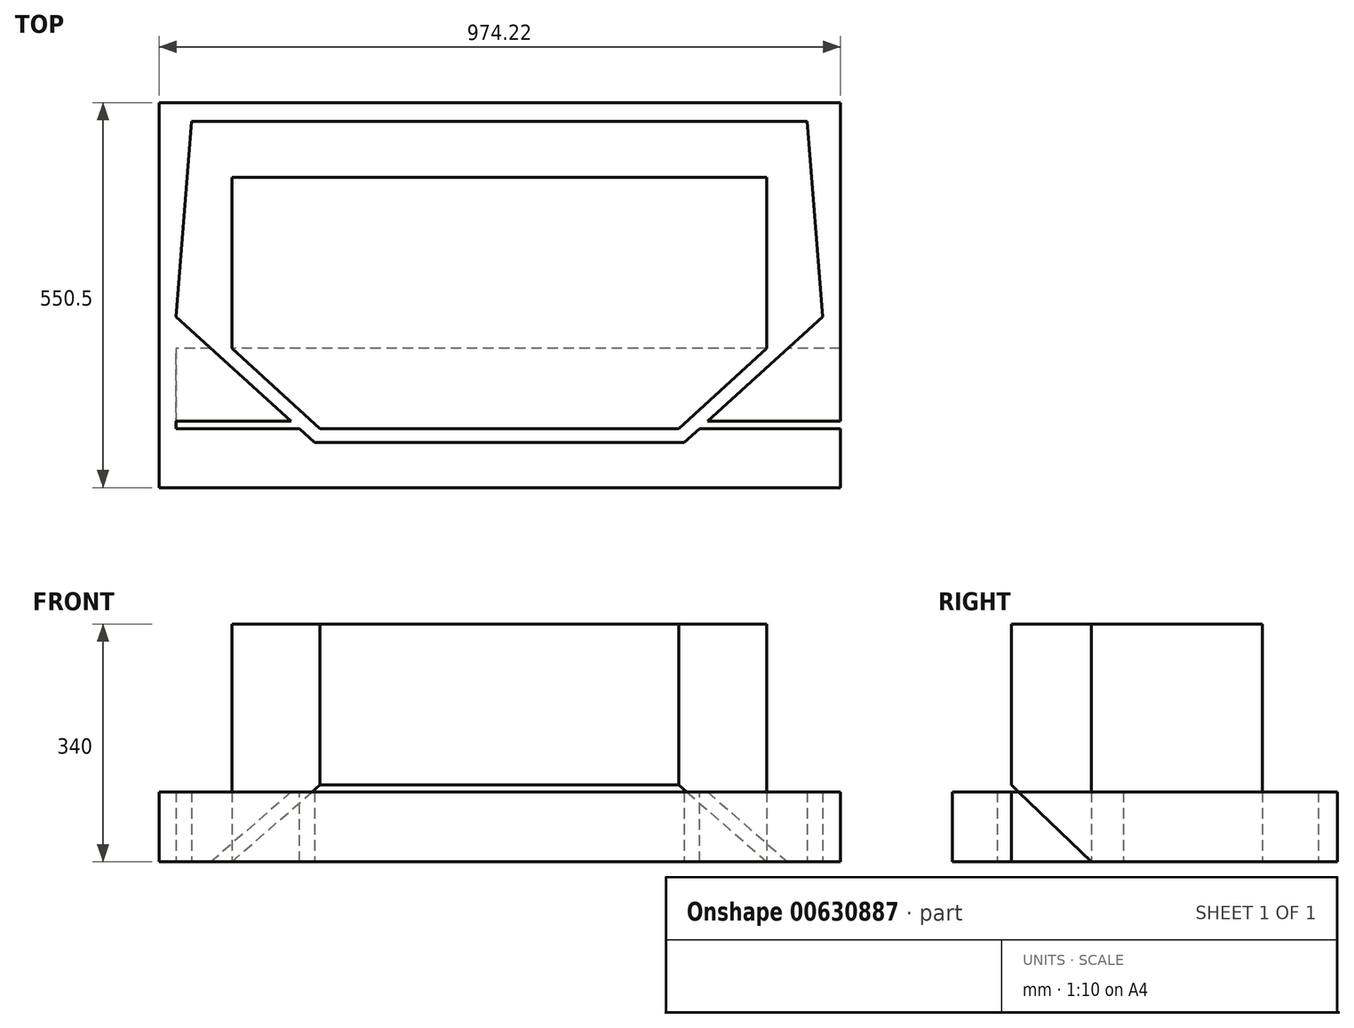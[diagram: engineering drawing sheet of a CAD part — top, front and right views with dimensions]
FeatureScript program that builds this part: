
annotation { "Feature Type Name" : "Feature", "Feature Type Description" : "" }
export const myFeature = defineFeature(function(context is Context, id is Id, definition is map)
    precondition{}
    {
        {
            var Q0;
            Q0=qCreatedBy(makeId("Top.planeOp"),FACE);
            var sketch = newSketch(context, id + "F0", { "sketchPlane" : qUnion([Q0])});
            skLineSegment(sketch, "E0.bottom", {"start": v(0, 0) * mm, "end": v(925, 0) * mm});
            skLineSegment(sketch, "E0.top", {"start": v(0, 494) * mm, "end": v(925, 494) * mm});
            skLineSegment(sketch, "E0.left", {"start": v(0, 0) * mm, "end": v(0, 494) * mm});
            skLineSegment(sketch, "E0.right", {"start": v(925, 0) * mm, "end": v(925, 494) * mm});
            skLineSegment(sketch, "E1", {"start": v(22.5, 494) * mm, "end": v(0, 214.9) * mm});
            skLineSegment(sketch, "E2", {"start": v(0, 214.9) * mm, "end": v(237.1, 0) * mm});
            skPoint(sketch, "E3", {"position": v(462.5, 494) * mm});
            skPoint(sketch, "E4", {"position": v(462.5, 0) * mm});
            skLineSegment(sketch, "E5", {"start": v(462.5, 494) * mm, "end": v(462.5, 0) * mm});
            skLineSegment(sketch, "E6.MirrorCS", {"start": v(902.5, 494) * mm, "end": v(925, 214.9) * mm});
            skLineSegment(sketch, "E7.MirrorCS", {"start": v(925, 214.9) * mm, "end": v(687.9, 0) * mm});
            skLineSegment(sketch, "E8", {"start": v(0, 379) * mm, "end": v(925, 379) * mm});
            skLineSegment(sketch, "E9", {"start": v(0, 312) * mm, "end": v(925, 312) * mm});
            skLineSegment(sketch, "E10", {"start": v(0, 35) * mm, "end": v(925, 35) * mm});
            skLineSegment(sketch, "E11.bottom", {"start": v(950.09, 520.94) * mm, "end": v(-24.13, 520.94) * mm});
            skLineSegment(sketch, "E11.top", {"start": v(950.09, -29.56) * mm, "end": v(-24.13, -29.56) * mm});
            skLineSegment(sketch, "E11.left", {"start": v(950.09, 520.94) * mm, "end": v(950.09, -29.56) * mm});
            skLineSegment(sketch, "E11.right", {"start": v(-24.13, 520.94) * mm, "end": v(-24.13, -29.56) * mm});
            skSolve(sketch);
        }
        {
            var Q0;
            Q0=makeQuery(id+"F0.imprint","IMPRINT",FACE,{"disambiguationData":[TD([[makeQuery(id+"F0.imprint","IMPRINT",EDGE,{"derivedFrom":sQuery(id+"F0.wireOp",EDGE,"E11.bottom")}),1.0]])]});
            var Q1;
            {var subQ0=sQuery(id+"F0.wireOp",EDGE,"E1");var subQ1=sQuery(id+"F0.wireOp",EDGE,"E0.top");var subQ2=makeQuery(id+"F0.imprint","INTERSECT",VERTEX,{"derivedFrom":[subQ1,subQ0]});Q1=makeQuery(id+"F0.imprint","IMPRINT",FACE,{"disambiguationData":[TD([[makeQuery(id+"F0.imprint","IMPRINT",EDGE,{"disambiguationData":[TD([[subQ2,1.0]])],"derivedFrom":subQ1}),-1.0]])]});}
            var Q2;
            {var subQ0=sQuery(id+"F0.wireOp",EDGE,"E0.right");var subQ1=sQuery(id+"F0.wireOp",EDGE,"E0.top");var subQ2=makeQuery(id+"F0.imprint","INTERSECT",VERTEX,{"derivedFrom":[subQ1,subQ0]});Q2=makeQuery(id+"F0.imprint","IMPRINT",FACE,{"disambiguationData":[TD([[makeQuery(id+"F0.imprint","IMPRINT",EDGE,{"disambiguationData":[TD([[subQ2,1.0]])],"derivedFrom":subQ1}),-1.0]])]});}
            var Q3;
            {var subQ0=sQuery(id+"F0.wireOp",EDGE,"E10");var subQ1=sQuery(id+"F0.wireOp",EDGE,"E0.right");var subQ2=makeQuery(id+"F0.imprint","INTERSECT",VERTEX,{"derivedFrom":[subQ1,subQ0]});Q3=makeQuery(id+"F0.imprint","IMPRINT",FACE,{"disambiguationData":[TD([[makeQuery(id+"F0.imprint","IMPRINT",EDGE,{"disambiguationData":[TD([[subQ2,1.0]])],"derivedFrom":subQ0}),1.0]])]});}
            var Q4;
            {var subQ0=sQuery(id+"F0.wireOp",EDGE,"E7.MirrorCS");var subQ1=sQuery(id+"F0.wireOp",EDGE,"E0.bottom");var subQ2=makeQuery(id+"F0.imprint","INTERSECT",VERTEX,{"derivedFrom":[subQ1,subQ0]});Q4=makeQuery(id+"F0.imprint","IMPRINT",FACE,{"disambiguationData":[TD([[makeQuery(id+"F0.imprint","IMPRINT",EDGE,{"disambiguationData":[TD([[subQ2,-1.0]])],"derivedFrom":subQ1}),1.0]])]});}
            var Q5;
            {var subQ0=sQuery(id+"F0.wireOp",EDGE,"E2");var subQ1=sQuery(id+"F0.wireOp",EDGE,"E0.bottom");var subQ2=makeQuery(id+"F0.imprint","INTERSECT",VERTEX,{"derivedFrom":[subQ1,subQ0]});Q5=makeQuery(id+"F0.imprint","IMPRINT",FACE,{"disambiguationData":[TD([[makeQuery(id+"F0.imprint","IMPRINT",EDGE,{"disambiguationData":[TD([[subQ2,1.0]])],"derivedFrom":subQ1}),1.0]])]});}
            var Q6;
            {var subQ0=sQuery(id+"F0.wireOp",EDGE,"E10");var subQ1=sQuery(id+"F0.wireOp",EDGE,"E0.left");var subQ2=makeQuery(id+"F0.imprint","INTERSECT",VERTEX,{"derivedFrom":[subQ1,subQ0]});Q6=makeQuery(id+"F0.imprint","IMPRINT",FACE,{"disambiguationData":[TD([[makeQuery(id+"F0.imprint","IMPRINT",EDGE,{"disambiguationData":[TD([[subQ2,-1.0]])],"derivedFrom":subQ0}),1.0]])]});}
            var Q7;
            {var subQ0=sQuery(id+"F0.wireOp",EDGE,"E8");var subQ1=sQuery(id+"F0.wireOp",EDGE,"E0.left");var subQ2=makeQuery(id+"F0.imprint","INTERSECT",VERTEX,{"derivedFrom":[subQ1,subQ0]});Q7=makeQuery(id+"F0.imprint","IMPRINT",FACE,{"disambiguationData":[TD([[makeQuery(id+"F0.imprint","IMPRINT",EDGE,{"disambiguationData":[TD([[subQ2,1.0]])],"derivedFrom":subQ1}),-1.0]])]});}
            var Q8;
            {var subQ0=sQuery(id+"F0.wireOp",EDGE,"E1");var subQ3=sQuery(id+"F0.wireOp",EDGE,"E9");var subQ5=makeQuery(id+"F0.imprint","INTERSECT",VERTEX,{"derivedFrom":[subQ0,subQ3]});Q8=makeQuery(id+"F0.imprint","IMPRINT",FACE,{"disambiguationData":[TD([[makeQuery(id+"F0.imprint","IMPRINT",EDGE,{"disambiguationData":[TD([[subQ5,1.0]])],"derivedFrom":subQ3}),-1.0]])]});}
            var Q9;
            {var subQ1=sQuery(id+"F0.wireOp",EDGE,"E0.right");var subQ3=sQuery(id+"F0.wireOp",EDGE,"E9");var subQ4=makeQuery(id+"F0.imprint","INTERSECT",VERTEX,{"derivedFrom":[subQ1,subQ3]});Q9=makeQuery(id+"F0.imprint","IMPRINT",FACE,{"disambiguationData":[TD([[makeQuery(id+"F0.imprint","IMPRINT",EDGE,{"disambiguationData":[TD([[subQ4,1.0]])],"derivedFrom":subQ3}),-1.0]])]});}
            var Q10;
            {var subQ0=sQuery(id+"F0.wireOp",EDGE,"E8");var subQ1=sQuery(id+"F0.wireOp",EDGE,"E0.right");var subQ2=makeQuery(id+"F0.imprint","INTERSECT",VERTEX,{"derivedFrom":[subQ1,subQ0]});Q10=makeQuery(id+"F0.imprint","IMPRINT",FACE,{"disambiguationData":[TD([[makeQuery(id+"F0.imprint","IMPRINT",EDGE,{"disambiguationData":[TD([[subQ2,1.0]])],"derivedFrom":subQ1}),1.0]])]});}
            var Q11;
            {var subQ0=sQuery(id+"F0.wireOp",EDGE,"E7.MirrorCS");var subQ1=sQuery(id+"F0.wireOp",EDGE,"E0.bottom");var subQ2=makeQuery(id+"F0.imprint","INTERSECT",VERTEX,{"derivedFrom":[subQ1,subQ0]});Q11=makeQuery(id+"F0.imprint","IMPRINT",FACE,{"disambiguationData":[TD([[makeQuery(id+"F0.imprint","IMPRINT",EDGE,{"disambiguationData":[TD([[subQ2,1.0]])],"derivedFrom":subQ1}),1.0]])]});}
            var Q12;
            {var subQ0=sQuery(id+"F0.wireOp",EDGE,"E2");var subQ1=sQuery(id+"F0.wireOp",EDGE,"E0.bottom");var subQ2=makeQuery(id+"F0.imprint","INTERSECT",VERTEX,{"derivedFrom":[subQ1,subQ0]});Q12=makeQuery(id+"F0.imprint","IMPRINT",FACE,{"disambiguationData":[TD([[makeQuery(id+"F0.imprint","IMPRINT",EDGE,{"disambiguationData":[TD([[subQ2,-1.0]])],"derivedFrom":subQ1}),1.0]])]});}
            extrude(context, id + "F1", {"entities" : qUnion([Q0, Q1, Q2, Q3, Q4, Q5, Q6, Q7, Q8, Q9, Q10, Q11, Q12]), "depth" : 100 * mm, "offsetDistance" : 25 * mm});
        }
        {
            var Q0;
            Q0=qCreatedBy(makeId("Top.planeOp"),FACE);
            var sketch = newSketch(context, id + "F2", { "sketchPlane" : qUnion([Q0])});
            skLineSegment(sketch, "E12", {"start": v(80, 414) * mm, "end": v(845, 414) * mm});
            skLineSegment(sketch, "E13", {"start": v(845, 169.39) * mm, "end": v(718.8, 55) * mm});
            skLineSegment(sketch, "E14", {"start": v(718.8, 55) * mm, "end": v(206.2, 55) * mm});
            skLineSegment(sketch, "E15", {"start": v(206.2, 55) * mm, "end": v(80, 169.39) * mm});
            skLineSegment(sketch, "E16", {"start": v(80, 414) * mm, "end": v(80, 169.39) * mm});
            skLineSegment(sketch, "E17", {"start": v(845, 414) * mm, "end": v(845, 169.39) * mm});
            skSolve(sketch);
        }
        {
            var Q0;
            Q0=makeQuery(id+"F2.imprint","IMPRINT",FACE,{"disambiguationData":[TD([[makeQuery(id+"F2.imprint","IMPRINT",EDGE,{"derivedFrom":sQuery(id+"F2.wireOp",EDGE,"E12")}),-1.0]])]});
            extrude(context, id + "F3", {"entities" : qUnion([Q0]), "depth" : 340 * mm, "offsetDistance" : 25 * mm});
        }
        {
            var Q0;
            Q0=qCreatedBy(makeId("Right.planeOp"),FACE);
            var sketch = newSketch(context, id + "F4", { "sketchPlane" : qUnion([Q0])});
            skLineSegment(sketch, "E18", {"start": v(169.39, 0) * mm, "end": v(55, 110) * mm});
            skLineSegment(sketch, "E19", {"start": v(55, 110) * mm, "end": v(55, 0) * mm});
            skLineSegment(sketch, "E20", {"start": v(55, 0) * mm, "end": v(169.39, 0) * mm});
            skSolve(sketch);
        }
        {
            var Q0;
            Q0 = qSketchRegion(id + "F4", true);
            extrude(context, id + "F5", {"entities" : qUnion([Q0]), "operationType" : NewBodyOperationType.REMOVE, "endBound" : BoundingType.THROUGH_ALL, "depth" : 25 * mm, "offsetDistance" : 25 * mm});
        }
    });
